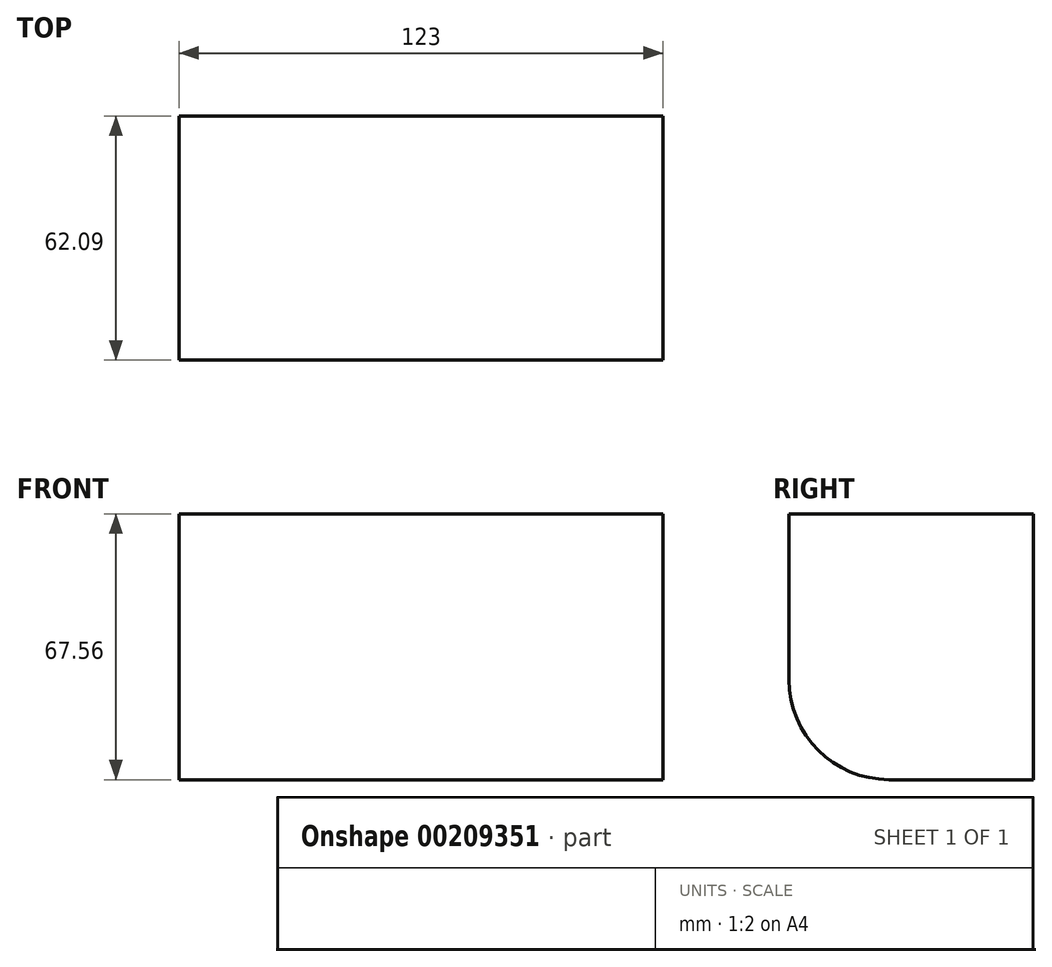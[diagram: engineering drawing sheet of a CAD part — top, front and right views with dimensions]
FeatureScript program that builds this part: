
annotation { "Feature Type Name" : "Feature", "Feature Type Description" : "" }
export const myFeature = defineFeature(function(context is Context, id is Id, definition is map)
    precondition{}
    {
        {
            var Q0;
            Q0=qCreatedBy(makeId("Top.planeOp"),FACE);
            var sketch = newSketch(context, id + "F0", { "sketchPlane" : qUnion([Q0])});
            skLineSegment(sketch, "E0.bottom", {"start": v(-60.92, 26.09) * mm, "end": v(62.08, 26.09) * mm});
            skLineSegment(sketch, "E0.top", {"start": v(-60.92, -36) * mm, "end": v(62.08, -36) * mm});
            skLineSegment(sketch, "E0.left", {"start": v(-60.92, 26.09) * mm, "end": v(-60.92, -36) * mm});
            skLineSegment(sketch, "E0.right", {"start": v(62.08, 26.09) * mm, "end": v(62.08, -36) * mm});
            skSolve(sketch);
        }
        {
            var Q0;
            Q0=makeQuery(id+"F0.imprint","IMPRINT",FACE,{"disambiguationData":[TD([[makeQuery(id+"F0.imprint","IMPRINT",EDGE,{"derivedFrom":sQuery(id+"F0.wireOp",EDGE,"E0.bottom")}),-1.0]])]});
            extrude(context, id + "F1", {"entities" : qUnion([Q0]), "depth" : 42.16 * mm});
        }
        {
            var Q0;
            Q0=makeQuery(id+"F1.opExtrude","CAP_EDGE",EDGE,{"disambiguationData":[OSD([sQuery(id+"F0.wireOp",EDGE,"E0.top")])],"isStart":true});
            fillet(context, id + "F2", {"entities" : qUnion([Q0]), "radius" : 25.4 * mm, "tangentPropagation" : true, "allowEdgeOverflow" : false});
        }
        {
            var Q0;
            Q0=makeQuery(id+"F1.opExtrude","CAP_FACE",FACE,{"disambiguationData":[OSD([sQuery(id+"F0.wireOp",EDGE,"E0.bottom"),sQuery(id+"F0.wireOp",EDGE,"E0.top"),sQuery(id+"F0.wireOp",EDGE,"E0.left"),sQuery(id+"F0.wireOp",EDGE,"E0.right")])],"isStart":false});
            extrude(context, id + "F3", {"entities" : qUnion([Q0]), "operationType" : NewBodyOperationType.ADD, "depth" : 25.4 * mm});
        }
    });
